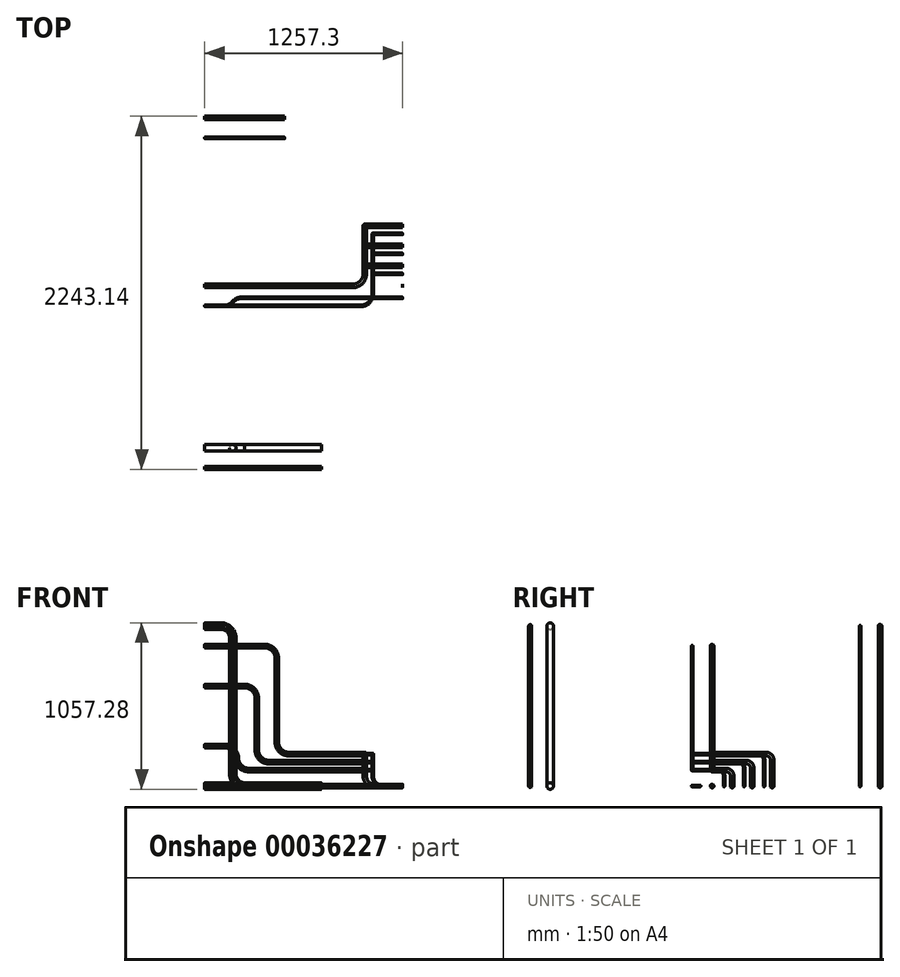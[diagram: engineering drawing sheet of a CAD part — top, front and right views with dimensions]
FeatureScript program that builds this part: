
annotation { "Feature Type Name" : "Feature", "Feature Type Description" : "" }
export const myFeature = defineFeature(function(context is Context, id is Id, definition is map)
    precondition{}
    {
        {
            var Q0;
            Q0=qCreatedBy(makeId("Right.planeOp"),FACE);
            var sketch = newSketch(context, id + "F0", { "sketchPlane" : qUnion([Q0])});
            skLineSegment(sketch, "E0.left", {"start": v(2095.5, 1016) * mm, "end": v(2095.5, 0) * mm, "construction": true});
            skLineSegment(sketch, "E1.left", {"start": v(0, 1016) * mm, "end": v(0, 0) * mm, "construction": true});
            skLineSegment(sketch, "E0.right", {"start": v(2222.5, 1016) * mm, "end": v(2222.5, 0) * mm, "construction": true});
            skLineSegment(sketch, "E1.right", {"start": v(127, 1016) * mm, "end": v(127, 0) * mm, "construction": true});
            skLineSegment(sketch, "E0.top", {"start": v(2095.5, 0) * mm, "end": v(2222.5, 0) * mm, "construction": true});
            skCircle(sketch, "E2", {"center": v(2095.5, 0) * mm, "radius": 4.76 * mm});
            skLineSegment(sketch, "E3.bottom", {"start": v(1028.7, 254) * mm, "end": v(1155.7, 254) * mm, "construction": true});
            skLineSegment(sketch, "E3.left", {"start": v(1028.7, 254) * mm, "end": v(1028.7, 0) * mm, "construction": true});
            skCircle(sketch, "E4", {"center": v(1028.7, 254) * mm, "radius": 4.76 * mm});
            skCircle(sketch, "E5", {"center": v(2222.5, 1016) * mm, "radius": 11.11 * mm});
            skLineSegment(sketch, "E3.top", {"start": v(1028.7, 0) * mm, "end": v(1155.7, 0) * mm, "construction": true});
            skCircle(sketch, "E6", {"center": v(127, 1016) * mm, "radius": 20.64 * mm});
            skCircle(sketch, "E7", {"center": v(1155.7, 0) * mm, "radius": 11.11 * mm});
            skCircle(sketch, "E8", {"center": v(1155.7, 254) * mm, "radius": 11.11 * mm});
            skLineSegment(sketch, "E9.bottom", {"start": v(1028.7, 889) * mm, "end": v(1155.7, 889) * mm, "construction": true});
            skLineSegment(sketch, "E0.bottom", {"start": v(2095.5, 1016) * mm, "end": v(2222.5, 1016) * mm, "construction": true});
            skLineSegment(sketch, "E3.right", {"start": v(1155.7, 254) * mm, "end": v(1155.7, 0) * mm, "construction": true});
            skCircle(sketch, "E10", {"center": v(127, 0) * mm, "radius": 20.64 * mm});
            skLineSegment(sketch, "E1.bottom", {"start": v(0, 1016) * mm, "end": v(127, 1016) * mm, "construction": true});
            skCircle(sketch, "E11", {"center": v(1155.7, 635) * mm, "radius": 11.11 * mm});
            skLineSegment(sketch, "E9.right", {"start": v(1155.7, 889) * mm, "end": v(1155.7, 635) * mm, "construction": true});
            skLineSegment(sketch, "E1.top", {"start": v(0, 0) * mm, "end": v(127, 0) * mm, "construction": true});
            skLineSegment(sketch, "E9.left", {"start": v(1028.7, 889) * mm, "end": v(1028.7, 635) * mm, "construction": true});
            skLineSegment(sketch, "E9.top", {"start": v(1028.7, 635) * mm, "end": v(1155.7, 635) * mm, "construction": true});
            skCircle(sketch, "E12", {"center": v(1028.7, 889) * mm, "radius": 4.76 * mm});
            skCircle(sketch, "E13", {"center": v(2095.5, 1016) * mm, "radius": 4.76 * mm});
            skCircle(sketch, "E14", {"center": v(2222.5, 0) * mm, "radius": 11.11 * mm});
            skCircle(sketch, "E15", {"center": v(1028.7, 0) * mm, "radius": 4.76 * mm});
            skCircle(sketch, "E16", {"center": v(1028.7, 635) * mm, "radius": 4.76 * mm});
            skCircle(sketch, "E17", {"center": v(1155.7, 889) * mm, "radius": 11.11 * mm});
            skCircle(sketch, "E18", {"center": v(0, 1016) * mm, "radius": 9.52 * mm});
            skCircle(sketch, "E19", {"center": v(0, 0) * mm, "radius": 9.53 * mm});
            skSolve(sketch);
        }
        {
            var Q0;
            Q0=qCreatedBy(makeId("Front.planeOp"),FACE);
            var sketch = newSketch(context, id + "F1", { "sketchPlane" : qUnion([Q0])});
            skLineSegment(sketch, "E20", {"start": v(0, 0) * mm, "end": v(739.94, 0) * mm});
            skLineSegment(sketch, "E21", {"start": v(0, 1016) * mm, "end": v(101.6, 1016) * mm});
            skArc(sketch, "E22", {"start": v(101.6, 1016) * mm, "mid": v(155.48, 993.68) * mm, "end": v(177.8, 939.8) * mm});
            skLineSegment(sketch, "E23", {"start": v(177.8, 939.8) * mm, "end": v(177.8, 76.2) * mm});
            skArc(sketch, "E24", {"start": v(177.8, 76.2) * mm, "mid": v(200.12, 22.32) * mm, "end": v(254, 0) * mm});
            skSolve(sketch);
        }
        {
            var Q0;
            Q0=makeQuery(id+"F0.imprint","IMPRINT",FACE,{"disambiguationData":[TD([[makeQuery(id+"F0.imprint","IMPRINT",EDGE,{"derivedFrom":sQuery(id+"F0.wireOp",EDGE,"E18")}),1.0]])]});
            var Q1;
            Q1=makeQuery(id+"F0.imprint","IMPRINT",FACE,{"disambiguationData":[TD([[makeQuery(id+"F0.imprint","IMPRINT",EDGE,{"derivedFrom":sQuery(id+"F0.wireOp",EDGE,"E6")}),1.0]])]});
            var Q2;
            Q2=sQuery(id+"F1.wireOp",EDGE,"E21");
            var Q3;
            Q3=sQuery(id+"F1.wireOp",EDGE,"E22");
            var Q4;
            Q4=sQuery(id+"F1.wireOp",EDGE,"E23");
            var Q5;
            Q5=sQuery(id+"F1.wireOp",EDGE,"E24");
            sweep(context, id + "F2", {"profiles" : qUnion([Q0, Q1]), "path" : qUnion([Q2, Q3, Q4, Q5])});
        }
        {
            var Q0;
            Q0=makeQuery(id+"F0.imprint","IMPRINT",FACE,{"disambiguationData":[TD([[makeQuery(id+"F0.imprint","IMPRINT",EDGE,{"derivedFrom":sQuery(id+"F0.wireOp",EDGE,"E19")}),1.0]])]});
            var Q1;
            Q1=makeQuery(id+"F0.imprint","IMPRINT",FACE,{"disambiguationData":[TD([[makeQuery(id+"F0.imprint","IMPRINT",EDGE,{"derivedFrom":sQuery(id+"F0.wireOp",EDGE,"E10")}),1.0]])]});
            var Q2;
            Q2=sQuery(id+"F1.wireOp",EDGE,"E20");
            sweep(context, id + "F3", {"profiles" : qUnion([Q0, Q1]), "path" : qUnion([Q2])});
        }
        {
            var Q0;
            Q0=qCreatedBy(makeId("Front.planeOp"),FACE);
            var Q1;
            Q1=sQuery(id+"F0.wireOp",VERTEX,"E0.top.start");
            cPlane(context, id + "F4", {"entities" : qUnion([Q0, Q1]), "cplaneType" : CPlaneType.PLANE_POINT, "offset" : 152.4 * mm, "width" : 152.4 * mm, "height" : 152.4 * mm});
        }
        {
            var Q0;
            Q0=qCreatedBy(id+"F4.planeOp",FACE);
            var sketch = newSketch(context, id + "F5", { "sketchPlane" : qUnion([Q0])});
            skLineSegment(sketch, "E25", {"start": v(177.8, 939.8) * mm, "end": v(177.8, 76.2) * mm});
            skArc(sketch, "E26", {"start": v(101.6, 1016) * mm, "mid": v(155.48, 993.68) * mm, "end": v(177.8, 939.8) * mm});
            skArc(sketch, "E27", {"start": v(177.8, 76.2) * mm, "mid": v(200.12, 22.32) * mm, "end": v(254, 0) * mm});
            skLineSegment(sketch, "E28", {"start": v(0, 0) * mm, "end": v(508, 0) * mm});
            skLineSegment(sketch, "E29", {"start": v(0, 1016) * mm, "end": v(101.6, 1016) * mm});
            skSolve(sketch);
        }
        {
            var Q0;
            Q0=makeQuery(id+"F0.imprint","IMPRINT",FACE,{"disambiguationData":[TD([[makeQuery(id+"F0.imprint","IMPRINT",EDGE,{"derivedFrom":sQuery(id+"F0.wireOp",EDGE,"E13")}),1.0]])]});
            var Q1;
            Q1=makeQuery(id+"F0.imprint","IMPRINT",FACE,{"disambiguationData":[TD([[makeQuery(id+"F0.imprint","IMPRINT",EDGE,{"derivedFrom":sQuery(id+"F0.wireOp",EDGE,"E5")}),1.0]])]});
            var Q2;
            Q2=sQuery(id+"F5.wireOp",EDGE,"E29");
            var Q3;
            Q3=sQuery(id+"F5.wireOp",EDGE,"E26");
            var Q4;
            Q4=sQuery(id+"F5.wireOp",EDGE,"E25");
            var Q5;
            Q5=sQuery(id+"F5.wireOp",EDGE,"E27");
            sweep(context, id + "F6", {"profiles" : qUnion([Q0, Q1]), "path" : qUnion([Q2, Q3, Q4, Q5])});
        }
        {
            var Q0;
            Q0=makeQuery(id+"F0.imprint","IMPRINT",FACE,{"disambiguationData":[TD([[makeQuery(id+"F0.imprint","IMPRINT",EDGE,{"derivedFrom":sQuery(id+"F0.wireOp",EDGE,"E2")}),1.0]])]});
            var Q1;
            Q1=makeQuery(id+"F0.imprint","IMPRINT",FACE,{"disambiguationData":[TD([[makeQuery(id+"F0.imprint","IMPRINT",EDGE,{"derivedFrom":sQuery(id+"F0.wireOp",EDGE,"E14")}),1.0]])]});
            var Q2;
            Q2=sQuery(id+"F5.wireOp",EDGE,"E28");
            sweep(context, id + "F7", {"profiles" : qUnion([Q0, Q1]), "path" : qUnion([Q2])});
        }
        {
            var Q0;
            Q0=qCreatedBy(makeId("Front.planeOp"),FACE);
            var Q1;
            Q1=sQuery(id+"F0.wireOp",VERTEX,"E15.center");
            cPlane(context, id + "F8", {"entities" : qUnion([Q0, Q1]), "cplaneType" : CPlaneType.PLANE_POINT, "offset" : 152.4 * mm, "width" : 152.4 * mm, "height" : 152.4 * mm});
        }
        {
            var Q0;
            Q0=qCreatedBy(id+"F8.planeOp",FACE);
            var sketch = newSketch(context, id + "F9", { "sketchPlane" : qUnion([Q0])});
            skLineSegment(sketch, "E30", {"start": v(0, 0) * mm, "end": v(127, 0) * mm});
            skLineSegment(sketch, "E31", {"start": v(0, 889) * mm, "end": v(381, 889) * mm});
            skArc(sketch, "E32", {"start": v(381, 889) * mm, "mid": v(434.88, 866.68) * mm, "end": v(457.2, 812.8) * mm});
            skLineSegment(sketch, "E33", {"start": v(457.2, 812.8) * mm, "end": v(457.2, 279.4) * mm});
            skLineSegment(sketch, "E34", {"start": v(0, 635) * mm, "end": v(254, 635) * mm});
            skArc(sketch, "E35", {"start": v(254, 635) * mm, "mid": v(307.88, 612.68) * mm, "end": v(330.2, 558.8) * mm});
            skLineSegment(sketch, "E36", {"start": v(330.2, 558.8) * mm, "end": v(330.2, 228.6) * mm});
            skLineSegment(sketch, "E37", {"start": v(0, 254) * mm, "end": v(127, 254) * mm});
            skArc(sketch, "E38", {"start": v(127, 254) * mm, "mid": v(180.88, 231.68) * mm, "end": v(203.2, 177.8) * mm});
            skLineSegment(sketch, "E39", {"start": v(203.2, 177.8) * mm, "end": v(203.2, 177.8) * mm});
            skArc(sketch, "E40", {"start": v(457.2, 279.4) * mm, "mid": v(479.52, 225.52) * mm, "end": v(533.4, 203.2) * mm});
            skArc(sketch, "E41", {"start": v(330.2, 228.6) * mm, "mid": v(352.52, 174.72) * mm, "end": v(406.4, 152.4) * mm});
            skArc(sketch, "E42", {"start": v(203.2, 177.8) * mm, "mid": v(225.52, 123.92) * mm, "end": v(279.4, 101.6) * mm});
            skLineSegment(sketch, "E43", {"start": v(279.4, 101.6) * mm, "end": v(939.8, 101.6) * mm});
            skLineSegment(sketch, "E44", {"start": v(406.4, 152.4) * mm, "end": v(939.8, 152.4) * mm});
            skLineSegment(sketch, "E45", {"start": v(533.4, 203.2) * mm, "end": v(939.8, 203.2) * mm});
            skLineSegment(sketch, "E46", {"start": v(406.4, 152.4) * mm, "end": v(406.4, 101.6) * mm, "construction": true});
            skLineSegment(sketch, "E47", {"start": v(533.4, 203.2) * mm, "end": v(533.4, 152.4) * mm, "construction": true});
            skLineSegment(sketch, "E48", {"start": v(279.4, 101.6) * mm, "end": v(279.4, 0) * mm, "construction": true});
            skLineSegment(sketch, "E49", {"start": v(939.8, 101.6) * mm, "end": v(939.8, 242.03) * mm, "construction": true});
            skLineSegment(sketch, "E50", {"start": v(127, 0) * mm, "end": v(127, 177.8) * mm, "construction": true});
            skLineSegment(sketch, "E51", {"start": v(127, 0) * mm, "end": v(1016, 0) * mm, "construction": true});
            skSolve(sketch);
        }
        {
            var Q0;
            Q0=makeQuery(id+"F0.imprint","IMPRINT",FACE,{"disambiguationData":[TD([[makeQuery(id+"F0.imprint","IMPRINT",EDGE,{"derivedFrom":sQuery(id+"F0.wireOp",EDGE,"E12")}),1.0]])]});
            var Q1;
            Q1=makeQuery(id+"F0.imprint","IMPRINT",FACE,{"disambiguationData":[TD([[makeQuery(id+"F0.imprint","IMPRINT",EDGE,{"derivedFrom":sQuery(id+"F0.wireOp",EDGE,"E17")}),1.0]])]});
            var Q2;
            Q2=sQuery(id+"F9.wireOp",EDGE,"E31");
            var Q3;
            Q3=sQuery(id+"F9.wireOp",EDGE,"E32");
            var Q4;
            Q4=sQuery(id+"F9.wireOp",EDGE,"E33");
            var Q5;
            Q5=sQuery(id+"F9.wireOp",EDGE,"E40");
            var Q6;
            Q6=sQuery(id+"F9.wireOp",EDGE,"E45");
            sweep(context, id + "F10", {"profiles" : qUnion([Q0, Q1]), "path" : qUnion([Q2, Q3, Q4, Q5, Q6])});
        }
        {
            var Q0;
            Q0=makeQuery(id+"F0.imprint","IMPRINT",FACE,{"disambiguationData":[TD([[makeQuery(id+"F0.imprint","IMPRINT",EDGE,{"derivedFrom":sQuery(id+"F0.wireOp",EDGE,"E16")}),1.0]])]});
            var Q1;
            Q1=makeQuery(id+"F0.imprint","IMPRINT",FACE,{"disambiguationData":[TD([[makeQuery(id+"F0.imprint","IMPRINT",EDGE,{"derivedFrom":sQuery(id+"F0.wireOp",EDGE,"E11")}),1.0]])]});
            var Q2;
            Q2=sQuery(id+"F9.wireOp",EDGE,"E34");
            var Q3;
            Q3=sQuery(id+"F9.wireOp",EDGE,"E35");
            var Q4;
            Q4=sQuery(id+"F9.wireOp",EDGE,"E36");
            var Q5;
            Q5=sQuery(id+"F9.wireOp",EDGE,"E41");
            var Q6;
            Q6=sQuery(id+"F9.wireOp",EDGE,"E44");
            sweep(context, id + "F11", {"profiles" : qUnion([Q0, Q1]), "path" : qUnion([Q2, Q3, Q4, Q5, Q6])});
        }
        {
            var Q0;
            Q0=makeQuery(id+"F0.imprint","IMPRINT",FACE,{"disambiguationData":[TD([[makeQuery(id+"F0.imprint","IMPRINT",EDGE,{"derivedFrom":sQuery(id+"F0.wireOp",EDGE,"E4")}),1.0]])]});
            var Q1;
            Q1=makeQuery(id+"F0.imprint","IMPRINT",FACE,{"disambiguationData":[TD([[makeQuery(id+"F0.imprint","IMPRINT",EDGE,{"derivedFrom":sQuery(id+"F0.wireOp",EDGE,"E8")}),1.0]])]});
            var Q2;
            Q2=sQuery(id+"F9.wireOp",EDGE,"E37");
            var Q3;
            Q3=sQuery(id+"F9.wireOp",EDGE,"E38");
            var Q4;
            Q4=sQuery(id+"F9.wireOp",EDGE,"E39");
            var Q5;
            Q5=sQuery(id+"F9.wireOp",EDGE,"E42");
            var Q6;
            Q6=sQuery(id+"F9.wireOp",EDGE,"E43");
            sweep(context, id + "F12", {"profiles" : qUnion([Q0, Q1]), "path" : qUnion([Q2, Q3, Q4, Q5, Q6])});
        }
        {
            var Q0;
            Q0=makeQuery(id+"F0.imprint","IMPRINT",FACE,{"disambiguationData":[TD([[makeQuery(id+"F0.imprint","IMPRINT",EDGE,{"derivedFrom":sQuery(id+"F0.wireOp",EDGE,"E15")}),1.0]])]});
            var Q1;
            Q1=sQuery(id+"F9.wireOp",EDGE,"E30");
            sweep(context, id + "F13", {"profiles" : qUnion([Q0]), "path" : qUnion([Q1])});
        }
        {
            var Q0;
            Q0=qCreatedBy(makeId("Top.planeOp"),FACE);
            var sketch = newSketch(context, id + "F14", { "sketchPlane" : qUnion([Q0])});
            skLineSegment(sketch, "E52", {"start": v(0, 1155.7) * mm, "end": v(1016, 1155.7) * mm});
            skLineSegment(sketch, "E53", {"start": v(1016, 1155.7) * mm, "end": v(1016, 1028.7) * mm, "construction": true});
            skSolve(sketch);
        }
        {
            var Q0;
            Q0=qCreatedBy(makeId("Top.planeOp"),FACE);
            var sketch = newSketch(context, id + "F15", { "sketchPlane" : qUnion([Q0])});
            skLineSegment(sketch, "E54", {"start": v(1016, 1028.7) * mm, "end": v(1016, 1079.5) * mm, "construction": true});
            skLineSegment(sketch, "E55", {"start": v(1016, 1079.5) * mm, "end": v(228.6, 1079.5) * mm});
            skArc(sketch, "E56", {"start": v(228.6, 1079.5) * mm, "mid": v(200.2, 1072.8) * mm, "end": v(177.8, 1054.1) * mm});
            skArc(sketch, "E57", {"start": v(177.8, 1054.1) * mm, "mid": v(155.4, 1035.4) * mm, "end": v(127, 1028.7) * mm});
            skSolve(sketch);
        }
        {
            var Q0;
            Q0=makeQuery(id+"F13.opSweep","CAP_FACE",FACE,{"disambiguationData":[OSD([sQuery(id+"F0.wireOp",EDGE,"E15"),sQuery(id+"F9.wireOp",VERTEX,"E30.end")])],"isStart":false});
            var Q1;
            Q1=sQuery(id+"F15.wireOp",EDGE,"E57");
            var Q2;
            Q2=sQuery(id+"F15.wireOp",EDGE,"E56");
            var Q3;
            Q3=sQuery(id+"F15.wireOp",EDGE,"E55");
            sweep(context, id + "F16", {"operationType" : NewBodyOperationType.ADD, "profiles" : qUnion([Q0]), "path" : qUnion([Q1, Q2, Q3])});
        }
        {
            var Q0;
            Q0=makeQuery(id+"F0.imprint","IMPRINT",FACE,{"disambiguationData":[TD([[makeQuery(id+"F0.imprint","IMPRINT",EDGE,{"derivedFrom":sQuery(id+"F0.wireOp",EDGE,"E7")}),1.0]])]});
            var Q1;
            Q1=sQuery(id+"F14.wireOp",EDGE,"E52");
            var Q2;
            Q2=sQuery(id+"F14.wireOp",EDGE,"4a2dfa43-30f4-475f-a33f-f8a94ffda145");
            var Q3;
            Q3=sQuery(id+"F14.wireOp",EDGE,"7a21a78b-97e9-4131-b010-21c43074d11a");
            var Q4;
            Q4=sQuery(id+"F14.wireOp",EDGE,"a07ae2be-8536-4233-b302-4f1de79af4b1");
            sweep(context, id + "F17", {"profiles" : qUnion([Q0]), "path" : qUnion([Q1, Q2, Q3, Q4])});
        }
        {
            var Q0;
            Q0=qCreatedBy(makeId("Top.planeOp"),FACE);
            var Q1;
            Q1=sQuery(id+"F9.wireOp",VERTEX,"E43.end");
            cPlane(context, id + "F18", {"entities" : qUnion([Q0, Q1]), "cplaneType" : CPlaneType.PLANE_POINT, "offset" : 152.4 * mm, "width" : 152.4 * mm, "height" : 152.4 * mm});
        }
        {
            var Q0;
            Q0=qCreatedBy(id+"F18.planeOp",FACE);
            var sketch = newSketch(context, id + "F19", { "sketchPlane" : qUnion([Q0])});
            skLineSegment(sketch, "E58", {"start": v(1066.8, 1193.8) * mm, "end": v(1066.8, 1104.9) * mm});
            skArc(sketch, "E59", {"start": v(1066.8, 1104.9) * mm, "mid": v(1044.48, 1051.02) * mm, "end": v(990.6, 1028.7) * mm});
            skLineSegment(sketch, "E60", {"start": v(990.6, 1028.7) * mm, "end": v(939.8, 1028.7) * mm});
            skLineSegment(sketch, "E61", {"start": v(1016, 1244.6) * mm, "end": v(1016, 1231.9) * mm});
            skArc(sketch, "E62", {"start": v(1016, 1231.9) * mm, "mid": v(993.68, 1178.02) * mm, "end": v(939.8, 1155.7) * mm});
            skLineSegment(sketch, "E63", {"start": v(939.8, 1155.7) * mm, "end": v(0, 1155.7) * mm, "construction": true});
            skSolve(sketch);
        }
        {
            var Q0;
            Q0=makeQuery(id+"F12.opSweep","CAP_FACE",FACE,{"disambiguationData":[OSD([sQuery(id+"F0.wireOp",EDGE,"E4"),sQuery(id+"F9.wireOp",VERTEX,"E43.end")])],"isStart":false});
            var Q1;
            Q1=makeQuery(id+"F11.opSweep","CAP_FACE",FACE,{"disambiguationData":[OSD([sQuery(id+"F0.wireOp",EDGE,"E16"),sQuery(id+"F9.wireOp",VERTEX,"E44.end")])],"isStart":false});
            var Q2;
            Q2=makeQuery(id+"F10.opSweep","CAP_FACE",FACE,{"disambiguationData":[OSD([sQuery(id+"F0.wireOp",EDGE,"E12"),sQuery(id+"F9.wireOp",VERTEX,"E45.end")])],"isStart":false});
            var Q3;
            Q3=sQuery(id+"F19.wireOp",EDGE,"E60");
            var Q4;
            Q4=sQuery(id+"F19.wireOp",EDGE,"E59");
            var Q5;
            Q5=sQuery(id+"F19.wireOp",EDGE,"E58");
            sweep(context, id + "F20", {"operationType" : NewBodyOperationType.ADD, "profiles" : qUnion([Q0, Q1, Q2]), "path" : qUnion([Q3, Q4, Q5])});
        }
        {
            var Q0;
            Q0=makeQuery(id+"F12.opSweep","CAP_FACE",FACE,{"disambiguationData":[OSD([sQuery(id+"F0.wireOp",EDGE,"E8"),sQuery(id+"F9.wireOp",VERTEX,"E43.end")])],"isStart":false});
            var Q1;
            Q1=makeQuery(id+"F11.opSweep","CAP_FACE",FACE,{"disambiguationData":[OSD([sQuery(id+"F0.wireOp",EDGE,"E11"),sQuery(id+"F9.wireOp",VERTEX,"E44.end")])],"isStart":false});
            var Q2;
            Q2=makeQuery(id+"F10.opSweep","CAP_FACE",FACE,{"disambiguationData":[OSD([sQuery(id+"F0.wireOp",EDGE,"E17"),sQuery(id+"F9.wireOp",VERTEX,"E45.end")])],"isStart":false});
            var Q3;
            Q3=sQuery(id+"F19.wireOp",EDGE,"E62");
            var Q4;
            Q4=sQuery(id+"F19.wireOp",EDGE,"E61");
            sweep(context, id + "F21", {"operationType" : NewBodyOperationType.ADD, "profiles" : qUnion([Q0, Q1, Q2]), "path" : qUnion([Q3, Q4])});
        }
        {
            var Q0;
            Q0=makeQuery(id+"F21.opSweep","CAP_FACE",FACE,{"disambiguationData":[OSD([sQuery(id+"F0.wireOp",EDGE,"E11"),sQuery(id+"F9.wireOp",VERTEX,"E44.end"),sQuery(id+"F19.wireOp",VERTEX,"E61.start")])],"isStart":false});
            var Q1;
            Q1=makeQuery(id+"F20.opSweep","CAP_FACE",FACE,{"disambiguationData":[OSD([sQuery(id+"F0.wireOp",EDGE,"E16"),sQuery(id+"F9.wireOp",VERTEX,"E44.end"),sQuery(id+"F19.wireOp",VERTEX,"E58.start")])],"isStart":false});
            extrude(context, id + "F22", {"entities" : qUnion([Q0, Q1]), "operationType" : NewBodyOperationType.ADD, "depth" : 127 * mm});
        }
        {
            var Q0;
            Q0=makeQuery(id+"F21.opSweep","CAP_FACE",FACE,{"disambiguationData":[OSD([sQuery(id+"F0.wireOp",EDGE,"E17"),sQuery(id+"F9.wireOp",VERTEX,"E45.end"),sQuery(id+"F19.wireOp",VERTEX,"E61.start")])],"isStart":false});
            var Q1;
            Q1=makeQuery(id+"F20.opSweep","CAP_FACE",FACE,{"disambiguationData":[OSD([sQuery(id+"F0.wireOp",EDGE,"E12"),sQuery(id+"F9.wireOp",VERTEX,"E45.end"),sQuery(id+"F19.wireOp",VERTEX,"E58.start")])],"isStart":false});
            extrude(context, id + "F23", {"entities" : qUnion([Q0, Q1]), "operationType" : NewBodyOperationType.ADD, "depth" : 254 * mm});
        }
        {
            var Q0;
            Q0=qCreatedBy(makeId("Right.planeOp"),FACE);
            var Q1;
            Q1=sQuery(id+"F19.wireOp",VERTEX,"E58.start");
            cPlane(context, id + "F24", {"entities" : qUnion([Q0, Q1]), "cplaneType" : CPlaneType.PLANE_POINT, "offset" : 152.4 * mm, "width" : 152.4 * mm, "height" : 152.4 * mm});
        }
        {
            var Q0;
            Q0=qCreatedBy(id+"F24.planeOp",FACE);
            var sketch = newSketch(context, id + "F25", { "sketchPlane" : qUnion([Q0])});
            skArc(sketch, "E64", {"start": v(1231.9, 63.5) * mm, "mid": v(1220.74, 90.44) * mm, "end": v(1193.8, 101.6) * mm});
            skLineSegment(sketch, "E65", {"start": v(1231.9, 63.5) * mm, "end": v(1159.71, 63.5) * mm, "construction": true});
            skArc(sketch, "E66", {"start": v(1358.9, 114.3) * mm, "mid": v(1347.74, 141.24) * mm, "end": v(1320.8, 152.4) * mm});
            skArc(sketch, "E67", {"start": v(1485.9, 165.1) * mm, "mid": v(1474.74, 192.04) * mm, "end": v(1447.8, 203.2) * mm});
            skLineSegment(sketch, "E68", {"start": v(1405.01, 152.4) * mm, "end": v(1320.8, 152.4) * mm, "construction": true});
            skLineSegment(sketch, "E69", {"start": v(1500.07, 203.2) * mm, "end": v(1447.8, 203.2) * mm, "construction": true});
            skLineSegment(sketch, "E70", {"start": v(1358.9, 114.3) * mm, "end": v(1320.8, 114.3) * mm, "construction": true});
            skLineSegment(sketch, "E71", {"start": v(1485.9, 165.1) * mm, "end": v(1447.8, 165.1) * mm, "construction": true});
            skLineSegment(sketch, "E72", {"start": v(1500.07, 203.2) * mm, "end": v(1500.07, 152.4) * mm, "construction": true});
            skLineSegment(sketch, "E73", {"start": v(1405.01, 152.4) * mm, "end": v(1405.01, 101.6) * mm, "construction": true});
            skLineSegment(sketch, "E74", {"start": v(1358.9, 114.3) * mm, "end": v(1358.9, 63.5) * mm});
            skLineSegment(sketch, "E75", {"start": v(1485.9, 165.1) * mm, "end": v(1485.9, 63.5) * mm});
            skSolve(sketch);
        }
        {
            var Q0;
            Q0=makeQuery(id+"F20.opSweep","CAP_FACE",FACE,{"disambiguationData":[OSD([sQuery(id+"F0.wireOp",EDGE,"E4"),sQuery(id+"F9.wireOp",VERTEX,"E43.end"),sQuery(id+"F19.wireOp",VERTEX,"E58.start")])],"isStart":false});
            var Q1;
            Q1=sQuery(id+"F25.wireOp",EDGE,"E64");
            sweep(context, id + "F26", {"operationType" : NewBodyOperationType.ADD, "profiles" : qUnion([Q0]), "path" : qUnion([Q1])});
        }
        {
            var Q0;
            Q0=makeQuery(id+"F22.opExtrude","CAP_FACE",FACE,{"disambiguationData":[OSD([sQuery(id+"F0.wireOp",EDGE,"E16"),sQuery(id+"F9.wireOp",VERTEX,"E44.end"),sQuery(id+"F19.wireOp",VERTEX,"E58.start")])],"isStart":false});
            var Q1;
            Q1=sQuery(id+"F25.wireOp",EDGE,"E66");
            var Q2;
            Q2=sQuery(id+"F25.wireOp",EDGE,"E74");
            sweep(context, id + "F27", {"operationType" : NewBodyOperationType.ADD, "profiles" : qUnion([Q0]), "path" : qUnion([Q1, Q2])});
        }
        {
            var Q0;
            Q0=makeQuery(id+"F23.opExtrude","CAP_FACE",FACE,{"disambiguationData":[OSD([sQuery(id+"F0.wireOp",EDGE,"E12"),sQuery(id+"F9.wireOp",VERTEX,"E45.end"),sQuery(id+"F19.wireOp",VERTEX,"E58.start")])],"isStart":false});
            var Q1;
            Q1=sQuery(id+"F25.wireOp",EDGE,"E67");
            var Q2;
            Q2=sQuery(id+"F25.wireOp",EDGE,"E75");
            sweep(context, id + "F28", {"operationType" : NewBodyOperationType.ADD, "profiles" : qUnion([Q0]), "path" : qUnion([Q1, Q2])});
        }
        {
            var Q0;
            Q0=qCreatedBy(id+"F24.planeOp",FACE);
            var Q1;
            Q1=sQuery(id+"F19.wireOp",VERTEX,"E61.start");
            cPlane(context, id + "F29", {"entities" : qUnion([Q0, Q1]), "cplaneType" : CPlaneType.PLANE_POINT, "offset" : 152.4 * mm, "width" : 152.4 * mm, "height" : 152.4 * mm});
        }
        {
            var Q0;
            Q0=qCreatedBy(id+"F29.planeOp",FACE);
            var sketch = newSketch(context, id + "F30", { "sketchPlane" : qUnion([Q0])});
            skArc(sketch, "E76", {"start": v(1282.7, 63.5) * mm, "mid": v(1271.54, 90.44) * mm, "end": v(1244.6, 101.6) * mm});
            skLineSegment(sketch, "E77", {"start": v(1282.7, 63.5) * mm, "end": v(1244.6, 63.5) * mm, "construction": true});
            skLineSegment(sketch, "E78", {"start": v(1371.6, 152.4) * mm, "end": v(1497.36, 152.4) * mm, "construction": true});
            skArc(sketch, "E79", {"start": v(1371.6, 152.4) * mm, "mid": v(1398.54, 141.24) * mm, "end": v(1409.7, 114.3) * mm});
            skLineSegment(sketch, "E80", {"start": v(1409.7, 114.3) * mm, "end": v(1409.7, 63.5) * mm});
            skLineSegment(sketch, "E81", {"start": v(1416.03, 203.2) * mm, "end": v(1498.6, 203.2) * mm, "construction": true});
            skArc(sketch, "E82", {"start": v(1498.6, 203.2) * mm, "mid": v(1525.54, 192.04) * mm, "end": v(1536.7, 165.1) * mm});
            skLineSegment(sketch, "E83", {"start": v(1536.7, 165.1) * mm, "end": v(1536.7, 63.5) * mm});
            skLineSegment(sketch, "E84", {"start": v(1371.6, 152.4) * mm, "end": v(1371.6, 101.6) * mm, "construction": true});
            skLineSegment(sketch, "E85", {"start": v(1498.6, 203.2) * mm, "end": v(1498.6, 152.4) * mm, "construction": true});
            skSolve(sketch);
        }
        {
            var Q0;
            Q0=makeQuery(id+"F21.opSweep","CAP_FACE",FACE,{"disambiguationData":[OSD([sQuery(id+"F0.wireOp",EDGE,"E8"),sQuery(id+"F9.wireOp",VERTEX,"E43.end"),sQuery(id+"F19.wireOp",VERTEX,"E61.start")])],"isStart":false});
            var Q1;
            Q1=sQuery(id+"F30.wireOp",EDGE,"E76");
            sweep(context, id + "F31", {"operationType" : NewBodyOperationType.ADD, "profiles" : qUnion([Q0]), "path" : qUnion([Q1])});
        }
        {
            var Q0;
            Q0=makeQuery(id+"F22.opExtrude","CAP_FACE",FACE,{"disambiguationData":[OSD([sQuery(id+"F0.wireOp",EDGE,"E11"),sQuery(id+"F9.wireOp",VERTEX,"E44.end"),sQuery(id+"F19.wireOp",VERTEX,"E61.start")])],"isStart":false});
            var Q1;
            Q1=sQuery(id+"F30.wireOp",EDGE,"E79");
            var Q2;
            Q2=sQuery(id+"F30.wireOp",EDGE,"E80");
            sweep(context, id + "F32", {"operationType" : NewBodyOperationType.ADD, "profiles" : qUnion([Q0]), "path" : qUnion([Q1, Q2])});
        }
        {
            var Q0;
            Q0=makeQuery(id+"F23.opExtrude","CAP_FACE",FACE,{"disambiguationData":[OSD([sQuery(id+"F0.wireOp",EDGE,"E17"),sQuery(id+"F9.wireOp",VERTEX,"E45.end"),sQuery(id+"F19.wireOp",VERTEX,"E61.start")])],"isStart":false});
            var Q1;
            Q1=sQuery(id+"F30.wireOp",EDGE,"E82");
            var Q2;
            Q2=sQuery(id+"F30.wireOp",EDGE,"E83");
            sweep(context, id + "F33", {"operationType" : NewBodyOperationType.ADD, "profiles" : qUnion([Q0]), "path" : qUnion([Q1, Q2])});
        }
        {
            var Q0;
            Q0=qCreatedBy(makeId("Front.planeOp"),FACE);
            var Q1;
            Q1=sQuery(id+"F25.wireOp",VERTEX,"E64.start");
            cPlane(context, id + "F34", {"entities" : qUnion([Q0, Q1]), "cplaneType" : CPlaneType.PLANE_POINT, "offset" : 152.4 * mm, "width" : 152.4 * mm, "height" : 152.4 * mm});
        }
        {
            var Q0;
            Q0=qCreatedBy(id+"F34.planeOp",FACE);
            var sketch = newSketch(context, id + "F35", { "sketchPlane" : qUnion([Q0])});
            skLineSegment(sketch, "E86", {"start": v(1257.3, 0) * mm, "end": v(1130.3, 0) * mm});
            skArc(sketch, "E87", {"start": v(1130.3, 0) * mm, "mid": v(1085.4, 18.6) * mm, "end": v(1066.8, 63.5) * mm});
            skLineSegment(sketch, "E88", {"start": v(1257.3, 0) * mm, "end": v(1079.5, 0) * mm});
            skArc(sketch, "E89", {"start": v(1079.5, 0) * mm, "mid": v(1034.6, 18.6) * mm, "end": v(1016, 63.5) * mm});
            skSolve(sketch);
        }
        {
            var Q0;
            Q0=makeQuery(id+"F26.opSweep","CAP_FACE",FACE,{"disambiguationData":[OSD([sQuery(id+"F0.wireOp",EDGE,"E4"),sQuery(id+"F9.wireOp",VERTEX,"E43.end"),sQuery(id+"F19.wireOp",VERTEX,"E58.start"),sQuery(id+"F25.wireOp",VERTEX,"E64.start")])],"isStart":false});
            var Q1;
            Q1=makeQuery(id+"F27.opSweep","CAP_FACE",FACE,{"disambiguationData":[OSD([sQuery(id+"F0.wireOp",EDGE,"E16"),sQuery(id+"F9.wireOp",VERTEX,"E44.end"),sQuery(id+"F19.wireOp",VERTEX,"E58.start"),sQuery(id+"F25.wireOp",VERTEX,"E74.end")])],"isStart":false});
            var Q2;
            Q2=makeQuery(id+"F28.opSweep","CAP_FACE",FACE,{"disambiguationData":[OSD([sQuery(id+"F0.wireOp",EDGE,"E12"),sQuery(id+"F9.wireOp",VERTEX,"E45.end"),sQuery(id+"F19.wireOp",VERTEX,"E58.start"),sQuery(id+"F25.wireOp",VERTEX,"E75.end")])],"isStart":false});
            var Q3;
            Q3=sQuery(id+"F35.wireOp",EDGE,"E87");
            var Q4;
            Q4=sQuery(id+"F35.wireOp",EDGE,"E86");
            sweep(context, id + "F36", {"operationType" : NewBodyOperationType.ADD, "profiles" : qUnion([Q0, Q1, Q2]), "path" : qUnion([Q3, Q4])});
        }
        {
            var Q0;
            Q0=makeQuery(id+"F31.opSweep","CAP_FACE",FACE,{"disambiguationData":[OSD([sQuery(id+"F0.wireOp",EDGE,"E8"),sQuery(id+"F9.wireOp",VERTEX,"E43.end"),sQuery(id+"F19.wireOp",VERTEX,"E61.start"),sQuery(id+"F30.wireOp",VERTEX,"E76.start")])],"isStart":false});
            var Q1;
            Q1=makeQuery(id+"F32.opSweep","CAP_FACE",FACE,{"disambiguationData":[OSD([sQuery(id+"F0.wireOp",EDGE,"E11"),sQuery(id+"F9.wireOp",VERTEX,"E44.end"),sQuery(id+"F19.wireOp",VERTEX,"E61.start"),sQuery(id+"F30.wireOp",VERTEX,"E80.end")])],"isStart":false});
            var Q2;
            Q2=makeQuery(id+"F33.opSweep","CAP_FACE",FACE,{"disambiguationData":[OSD([sQuery(id+"F0.wireOp",EDGE,"E17"),sQuery(id+"F9.wireOp",VERTEX,"E45.end"),sQuery(id+"F19.wireOp",VERTEX,"E61.start"),sQuery(id+"F30.wireOp",VERTEX,"E83.end")])],"isStart":false});
            var Q3;
            Q3=sQuery(id+"F35.wireOp",EDGE,"E89");
            var Q4;
            Q4=sQuery(id+"F35.wireOp",EDGE,"E88");
            sweep(context, id + "F37", {"operationType" : NewBodyOperationType.ADD, "profiles" : qUnion([Q0, Q1, Q2]), "path" : qUnion([Q3, Q4])});
        }
        {
            var Q0;
            Q0=makeQuery(id+"F16.opSweep","CAP_FACE",FACE,{"disambiguationData":[OSD([sQuery(id+"F0.wireOp",EDGE,"E15"),sQuery(id+"F9.wireOp",VERTEX,"E30.end"),sQuery(id+"F15.wireOp",VERTEX,"E55.start")])],"isStart":false});
            var Q1;
            Q1=makeQuery(id+"F17.opSweep","CAP_FACE",FACE,{"disambiguationData":[OSD([sQuery(id+"F0.wireOp",EDGE,"E7"),sQuery(id+"F14.wireOp",VERTEX,"E52.end")])],"isStart":false});
            extrude(context, id + "F38", {"entities" : qUnion([Q0, Q1]), "operationType" : NewBodyOperationType.ADD, "depth" : 241.3 * mm});
        }
    });
